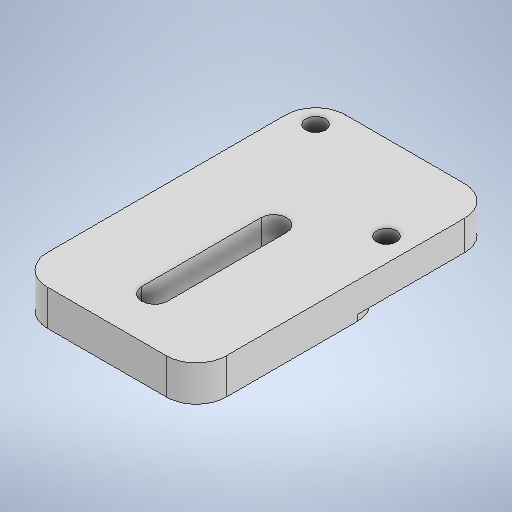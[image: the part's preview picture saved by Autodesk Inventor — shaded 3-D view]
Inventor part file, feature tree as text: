
AUTODESK INVENTOR PART (.ipt)
format: ipt  version: 2025.2 (Build 292293000, 293)  size: 259,072 bytes
history: native  units: mm
features: extrude x3, sketch x3, fillet x2
ambient origin geometry x8: Origin, YZ Plane, XZ Plane, XY Plane, X Axis, Y Axis, Z Axis, Center Point
bodies: Solid1 (feature_tree)
feature tree (8):
  extrude  "Extrusion1"  Depth=50.0mm
  fillet  "Fillet1"  Radius=5.0mm
  sketch  "Sketch2"  dims[d4=5.0mm d5=3.9mm d6=11.1mm]
  extrude  "Extrusion2"  Depth=5.0mm
  fillet  "Fillet2"  Radius=11.1mm
  extrude  "Extrusion3"  Depth=5.0mm
  sketch  "Sketch1"  dims[d0=30.0mm d1=50.0mm d2=5.0mm d3=0.0mm]
  sketch  "Sketch3"  dims[d7=22.2mm d8=10.3mm d9=3.3mm d10=3.3mm d11=8.0mm d12=4.3mm d13=20.0mm d14=4.3mm d15=32.0mm d16=1.0mm d17=0.0mm d18=5.0mm d19=0.0mm d20=0.0mm]
